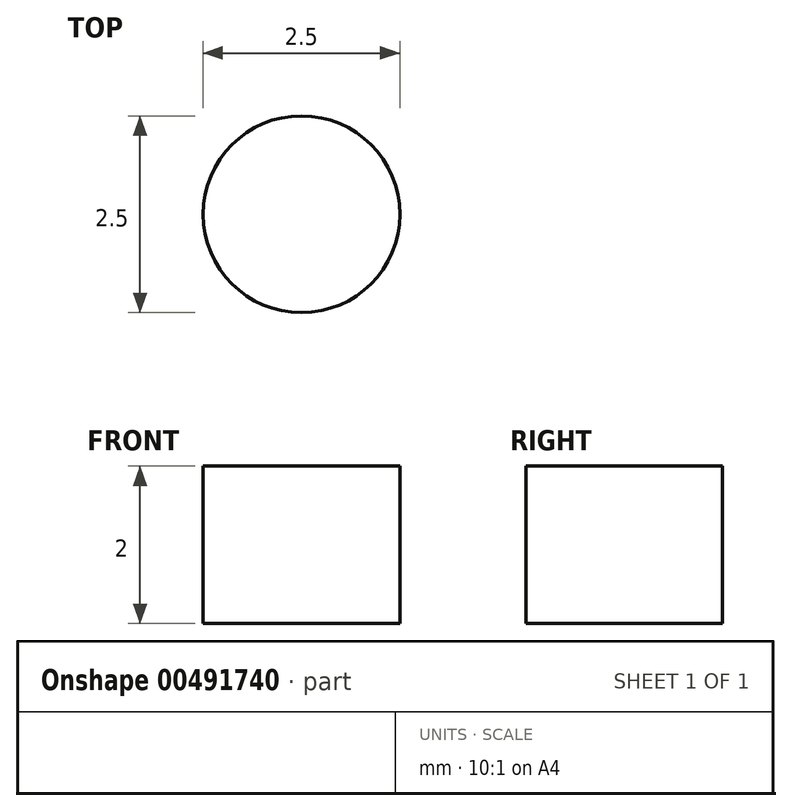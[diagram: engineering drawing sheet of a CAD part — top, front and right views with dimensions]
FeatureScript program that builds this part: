
annotation { "Feature Type Name" : "Feature", "Feature Type Description" : "" }
export const myFeature = defineFeature(function(context is Context, id is Id, definition is map)
    precondition{}
    {
        {
            var Q0;
            Q0=qCreatedBy(makeId("Top.planeOp"),FACE);
            var sketch = newSketch(context, id + "F0", { "sketchPlane" : qUnion([Q0])});
            skLineSegment(sketch, "E0.bottom", {"start": v(20.5, -7.5) * mm, "end": v(-20.5, -7.5) * mm});
            skLineSegment(sketch, "E0.top", {"start": v(20.5, 7.5) * mm, "end": v(-20.5, 7.5) * mm});
            skLineSegment(sketch, "E0.left", {"start": v(20.5, -7.5) * mm, "end": v(20.5, 7.5) * mm});
            skLineSegment(sketch, "E0.right", {"start": v(-20.5, -7.5) * mm, "end": v(-20.5, 7.5) * mm});
            skPoint(sketch, "E0.middle", {"position": v(0, 0) * mm});
            skSolve(sketch);
        }
        {
            var Q0;
            Q0=makeQuery(id+"F0.imprint","IMPRINT",FACE,{"disambiguationData":[TD([[makeQuery(id+"F0.imprint","IMPRINT",EDGE,{"derivedFrom":sQuery(id+"F0.wireOp",EDGE,"E0.bottom")}),-1.0]])]});
            extrude(context, id + "F1", {"entities" : qUnion([Q0]), "depth" : 2 * mm});
        }
        {
            var Q0;
            Q0=makeQuery(id+"F1.opExtrude","CAP_FACE",FACE,{"disambiguationData":[OSD([sQuery(id+"F0.wireOp",EDGE,"E0.bottom"),sQuery(id+"F0.wireOp",EDGE,"E0.top"),sQuery(id+"F0.wireOp",EDGE,"E0.left"),sQuery(id+"F0.wireOp",EDGE,"E0.right")])],"isStart":false});
            var sketch = newSketch(context, id + "F2", { "sketchPlane" : qUnion([Q0])});
            skLineSegment(sketch, "E1", {"start": v(20.5, 0) * mm, "end": v(-20.5, 0) * mm});
            skCircle(sketch, "E2", {"center": v(-17, 0) * mm, "radius": 1.25 * mm});
            skCircle(sketch, "E3", {"center": v(17, 0) * mm, "radius": 1.25 * mm});
            skSolve(sketch);
        }
        {
            var Q0;
            {var subQ0=sQuery(id+"F2.wireOp",EDGE,"E2");var subQ1=sQuery(id+"F2.wireOp",EDGE,"E1");var subQ2=makeQuery(id+"F2.imprint","INTERSECT",VERTEX,{"disambiguationData":[OD(0.0)],"derivedFrom":[subQ1,subQ0]});Q0=makeQuery(id+"F2.imprint","IMPRINT",FACE,{"disambiguationData":[TD([[makeQuery(id+"F2.imprint","IMPRINT",EDGE,{"disambiguationData":[TD([[subQ2,-1.0]])],"derivedFrom":subQ1}),-1.0]])]});}
            var Q1;
            {var subQ0=sQuery(id+"F2.wireOp",EDGE,"E2");var subQ1=sQuery(id+"F2.wireOp",EDGE,"E1");var subQ2=makeQuery(id+"F2.imprint","INTERSECT",VERTEX,{"disambiguationData":[OD(0.0)],"derivedFrom":[subQ1,subQ0]});Q1=makeQuery(id+"F2.imprint","IMPRINT",FACE,{"disambiguationData":[TD([[makeQuery(id+"F2.imprint","IMPRINT",EDGE,{"disambiguationData":[TD([[subQ2,-1.0]])],"derivedFrom":subQ1}),1.0]])]});}
            var Q2;
            {var subQ0=sQuery(id+"F2.wireOp",EDGE,"E3");var subQ1=sQuery(id+"F2.wireOp",EDGE,"E1");var subQ2=makeQuery(id+"F2.imprint","INTERSECT",VERTEX,{"disambiguationData":[OD(0.0)],"derivedFrom":[subQ1,subQ0]});Q2=makeQuery(id+"F2.imprint","IMPRINT",FACE,{"disambiguationData":[TD([[makeQuery(id+"F2.imprint","IMPRINT",EDGE,{"disambiguationData":[TD([[subQ2,-1.0]])],"derivedFrom":subQ1}),-1.0]])]});}
            var Q3;
            {var subQ0=sQuery(id+"F2.wireOp",EDGE,"E3");var subQ1=sQuery(id+"F2.wireOp",EDGE,"E1");var subQ2=makeQuery(id+"F2.imprint","INTERSECT",VERTEX,{"disambiguationData":[OD(0.0)],"derivedFrom":[subQ1,subQ0]});Q3=makeQuery(id+"F2.imprint","IMPRINT",FACE,{"disambiguationData":[TD([[makeQuery(id+"F2.imprint","IMPRINT",EDGE,{"disambiguationData":[TD([[subQ2,-1.0]])],"derivedFrom":subQ1}),1.0]])]});}
            extrude(context, id + "F3", {"entities" : qUnion([Q0, Q1, Q2, Q3]), "operationType" : NewBodyOperationType.REMOVE, "endBound" : BoundingType.THROUGH_ALL, "oppositeDirection" : true, "depth" : 25 * mm});
        }
    });
